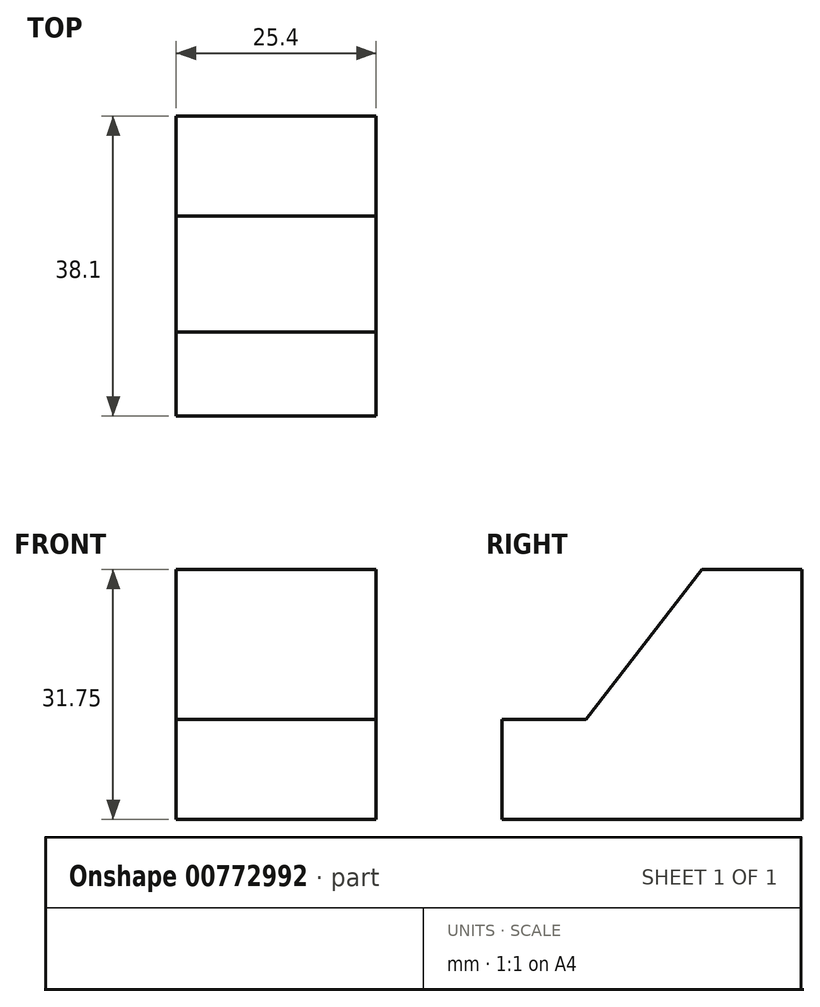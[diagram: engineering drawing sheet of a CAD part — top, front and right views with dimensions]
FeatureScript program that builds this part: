
annotation { "Feature Type Name" : "Feature", "Feature Type Description" : "" }
export const myFeature = defineFeature(function(context is Context, id is Id, definition is map)
    precondition{}
    {
        {
            var Q0;
            Q0=qCreatedBy(makeId("Right.planeOp"),FACE);
            var sketch = newSketch(context, id + "F0", { "sketchPlane" : qUnion([Q0])});
            skLineSegment(sketch, "E0", {"start": v(0, 0) * mm, "end": v(0, 31.75) * mm});
            skLineSegment(sketch, "E1", {"start": v(0, 31.75) * mm, "end": v(-12.7, 31.75) * mm});
            skLineSegment(sketch, "E2", {"start": v(0, 0) * mm, "end": v(-38.1, 0) * mm});
            skLineSegment(sketch, "E3", {"start": v(-38.1, 0) * mm, "end": v(-38.1, 12.7) * mm});
            skLineSegment(sketch, "E4", {"start": v(-40.15, 12.7) * mm, "end": v(-27.45, 12.7) * mm});
            skLineSegment(sketch, "E5", {"start": v(-12.7, 31.75) * mm, "end": v(-27.45, 12.7) * mm});
            skSolve(sketch);
        }
        {
            var Q0;
            Q0=makeQuery(id+"F0.imprint","IMPRINT",FACE,{"disambiguationData":[TD([[makeQuery(id+"F0.imprint","IMPRINT",EDGE,{"derivedFrom":sQuery(id+"F0.wireOp",EDGE,"E0")}),1.0]])]});
            extrude(context, id + "F1", {"entities" : qUnion([Q0]), "depth" : 25.4 * mm, "offsetDistance" : 25.4 * mm});
        }
    });
